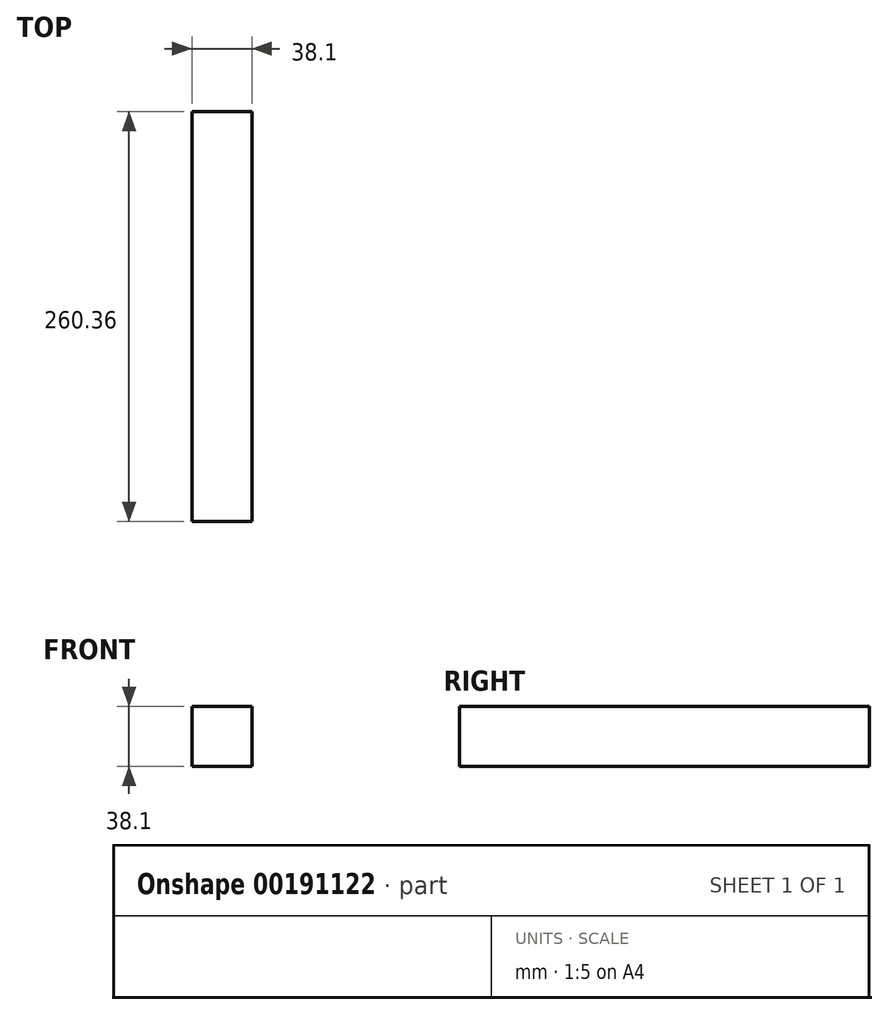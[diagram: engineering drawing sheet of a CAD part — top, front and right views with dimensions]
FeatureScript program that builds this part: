
annotation { "Feature Type Name" : "Feature", "Feature Type Description" : "" }
export const myFeature = defineFeature(function(context is Context, id is Id, definition is map)
    precondition{}
    {
        {
            var Q0;
            Q0=qCreatedBy(makeId("Front.planeOp"),FACE);
            var sketch = newSketch(context, id + "F0", { "sketchPlane" : qUnion([Q0])});
            skLineSegment(sketch, "E0.bottom", {"start": v(19.05, 19.05) * mm, "end": v(-19.05, 19.05) * mm});
            skLineSegment(sketch, "E0.top", {"start": v(19.05, -19.05) * mm, "end": v(-19.05, -19.05) * mm});
            skLineSegment(sketch, "E0.left", {"start": v(19.05, 19.05) * mm, "end": v(19.05, -19.05) * mm});
            skLineSegment(sketch, "E0.right", {"start": v(-19.05, 19.05) * mm, "end": v(-19.05, -19.05) * mm});
            skPoint(sketch, "E0.middle", {"position": v(0, 0) * mm});
            skSolve(sketch);
        }
        {
            var Q0;
            Q0 = qSketchRegion(id + "F0", true);
            extrude(context, id + "F1", {"entities" : qUnion([Q0]), "endBound" : BoundingType.SYMMETRIC, "depth" : 260.35 * mm});
        }
    });
